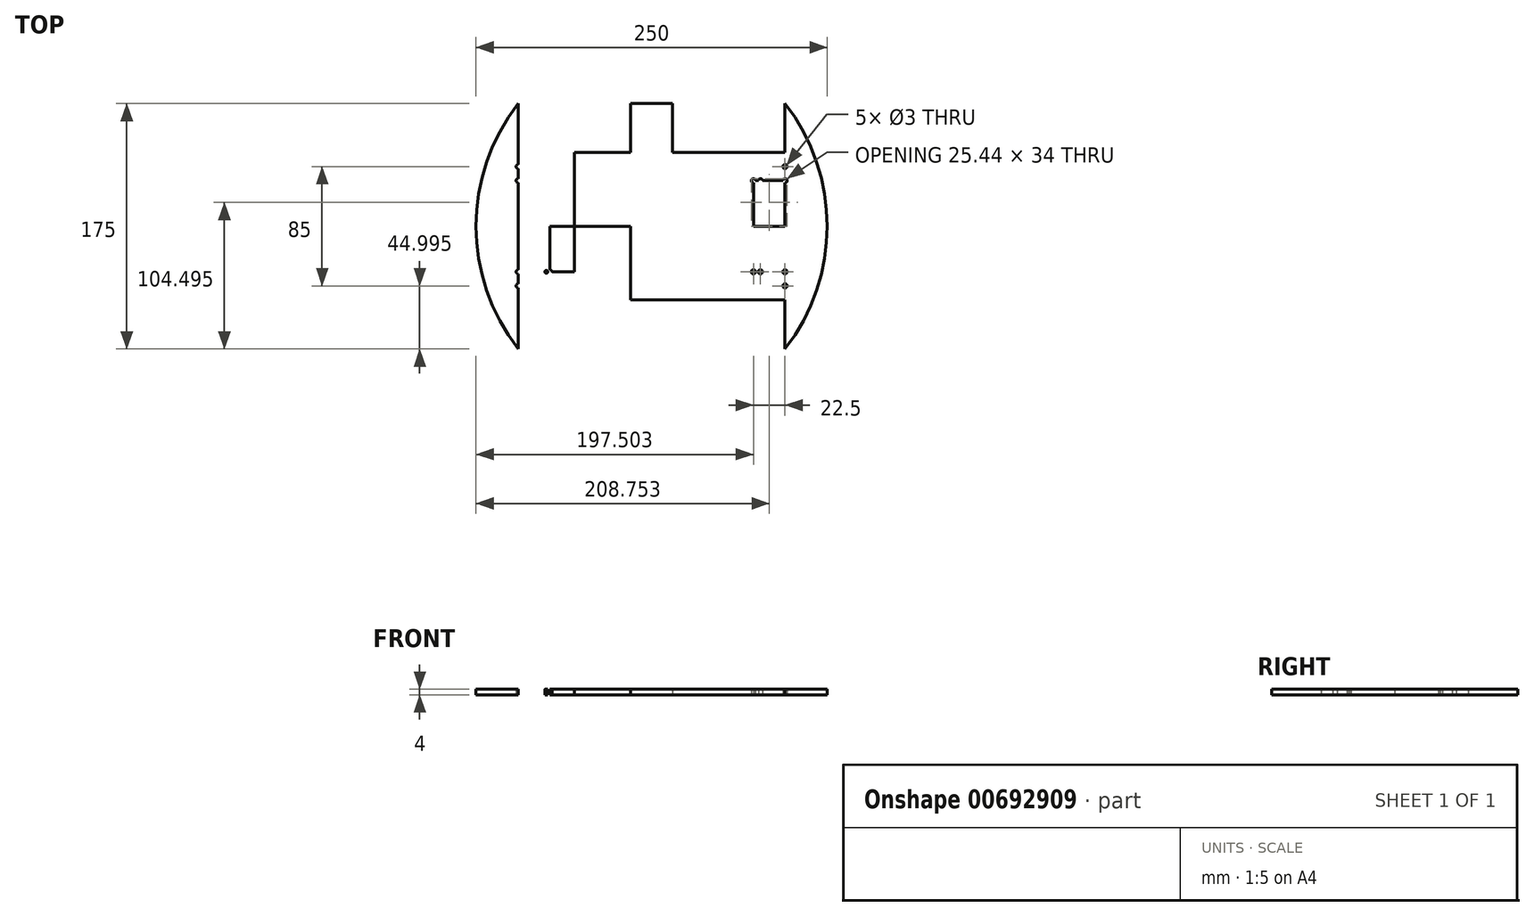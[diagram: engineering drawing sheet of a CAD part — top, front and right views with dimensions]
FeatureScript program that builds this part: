
annotation { "Feature Type Name" : "Feature", "Feature Type Description" : "" }
export const myFeature = defineFeature(function(context is Context, id is Id, definition is map)
    precondition{}
    {
        {
            var Q0;
            Q0=qCreatedBy(makeId("Top.planeOp"),FACE);
            var sketch = newSketch(context, id + "F0", { "sketchPlane" : qUnion([Q0])});
            skLineSegment(sketch, "E0", {"start": v(-125.28, 50.29) * mm, "end": v(-45.28, 50.29) * mm});
            skLineSegment(sketch, "E1", {"start": v(-45.28, 50.29) * mm, "end": v(-45.28, 85.29) * mm});
            skLineSegment(sketch, "E2", {"start": v(-45.28, 85.29) * mm, "end": v(-15.28, 85.29) * mm});
            skLineSegment(sketch, "E3", {"start": v(-15.28, 85.29) * mm, "end": v(-15.28, 50.29) * mm});
            skLineSegment(sketch, "E4", {"start": v(-15.28, 50.29) * mm, "end": v(64.72, 50.29) * mm});
            skLineSegment(sketch, "E5", {"start": v(64.72, 50.29) * mm, "end": v(64.72, 85.29) * mm});
            skLineSegment(sketch, "E6", {"start": v(-125.28, 50.29) * mm, "end": v(-125.28, 85.29) * mm});
            skLineSegment(sketch, "E7", {"start": v(-45.28, -54.71) * mm, "end": v(-45.28, 50.29) * mm});
            skLineSegment(sketch, "E8", {"start": v(-45.28, -54.71) * mm, "end": v(-125.28, -54.71) * mm});
            skLineSegment(sketch, "E9", {"start": v(-125.28, -54.71) * mm, "end": v(-125.28, 50.29) * mm});
            skLineSegment(sketch, "E10", {"start": v(-15.28, 50.29) * mm, "end": v(-15.28, -54.71) * mm});
            skLineSegment(sketch, "E11", {"start": v(-15.28, -54.71) * mm, "end": v(-45.28, -54.71) * mm});
            skLineSegment(sketch, "E12", {"start": v(-45.28, 50.29) * mm, "end": v(-15.28, 50.29) * mm});
            skLineSegment(sketch, "E13", {"start": v(64.72, 50.29) * mm, "end": v(64.72, -54.71) * mm});
            skLineSegment(sketch, "E14", {"start": v(64.72, -54.71) * mm, "end": v(-15.28, -54.71) * mm});
            skLineSegment(sketch, "E15.bottom", {"start": v(-45.28, -54.71) * mm, "end": v(-15.33, -54.71) * mm});
            skLineSegment(sketch, "E15.top", {"start": v(-45.28, -89.71) * mm, "end": v(-15.33, -89.71) * mm});
            skLineSegment(sketch, "E15.left", {"start": v(-45.28, -54.71) * mm, "end": v(-45.28, -89.71) * mm});
            skLineSegment(sketch, "E15.right", {"start": v(-15.33, -54.71) * mm, "end": v(-15.33, -89.71) * mm});
            skLineSegment(sketch, "E16", {"start": v(-125.28, -54.71) * mm, "end": v(-125.28, -89.71) * mm});
            skArc(sketch, "E17", {"start": v(-125.28, 85.29) * mm, "mid": v(-155.28, -2.21) * mm, "end": v(-125.28, -89.71) * mm});
            skLineSegment(sketch, "E18", {"start": v(64.72, -54.71) * mm, "end": v(64.72, -89.71) * mm});
            skArc(sketch, "E19", {"start": v(64.72, -89.71) * mm, "mid": v(94.72, -2.21) * mm, "end": v(64.72, 85.29) * mm});
            skLineSegment(sketch, "E20", {"start": v(-125.28, -54.71) * mm, "end": v(-85.28, -54.71) * mm});
            skLineSegment(sketch, "E21", {"start": v(-85.28, -54.71) * mm, "end": v(-45.28, -54.71) * mm});
            skLineSegment(sketch, "E22", {"start": v(-85.28, -54.71) * mm, "end": v(-85.28, 50.29) * mm});
            skLineSegment(sketch, "E23", {"start": v(-85.28, 50.29) * mm, "end": v(-45.28, 50.29) * mm});
            skLineSegment(sketch, "E24", {"start": v(-85.28, 50.29) * mm, "end": v(-125.28, 50.29) * mm});
            skLineSegment(sketch, "E25", {"start": v(-85.28, -54.71) * mm, "end": v(-85.28, -34.71) * mm});
            skLineSegment(sketch, "E26", {"start": v(-85.28, -34.71) * mm, "end": v(-105.28, -34.71) * mm});
            skCircle(sketch, "E27", {"center": v(-105.28, -34.71) * mm, "radius": 1 * mm});
            skPoint(sketch, "E28", {"position": v(-104.28, -34.71) * mm});
            skLineSegment(sketch, "E29", {"start": v(-104.28, -34.71) * mm, "end": v(-102.78, -34.71) * mm});
            skCircle(sketch, "E30", {"center": v(-102.78, -34.71) * mm, "radius": 1.5 * mm});
            skLineSegment(sketch, "E31", {"start": v(-105.28, -34.71) * mm, "end": v(-106.28, -34.71) * mm});
            skLineSegment(sketch, "E32", {"start": v(-106.28, -34.71) * mm, "end": v(-107.78, -34.71) * mm});
            skCircle(sketch, "E33", {"center": v(-107.78, -34.71) * mm, "radius": 1.5 * mm});
            skLineSegment(sketch, "E34", {"start": v(-30.28, 50.29) * mm, "end": v(-30.28, -2.21) * mm});
            skLineSegment(sketch, "E35", {"start": v(-30.28, -2.21) * mm, "end": v(-155.28, -2.21) * mm});
            skLineSegment(sketch, "E36", {"start": v(-30.28, -2.21) * mm, "end": v(94.72, -2.21) * mm});
            skLineSegment(sketch, "E37", {"start": v(94.72, -2.21) * mm, "end": v(-155.28, -2.21) * mm});
            skLineSegment(sketch, "E38", {"start": v(-107.78, -34.71) * mm, "end": v(-107.78, 30.29) * mm});
            skCircle(sketch, "E39", {"center": v(-107.78, 30.29) * mm, "radius": 1.5 * mm});
            skLineSegment(sketch, "E40", {"start": v(-102.78, -34.71) * mm, "end": v(-102.78, 30.29) * mm});
            skCircle(sketch, "E41", {"center": v(-102.78, 30.29) * mm, "radius": 1.5 * mm});
            skLineSegment(sketch, "E42", {"start": v(64.72, 50.29) * mm, "end": v(64.72, 30.29) * mm});
            skLineSegment(sketch, "E43", {"start": v(64.72, 30.29) * mm, "end": v(47.22, 30.29) * mm});
            skCircle(sketch, "E44", {"center": v(47.22, 30.29) * mm, "radius": 1.5 * mm});
            skLineSegment(sketch, "E45", {"start": v(47.22, 30.29) * mm, "end": v(42.22, 30.29) * mm});
            skCircle(sketch, "E46", {"center": v(42.22, 30.29) * mm, "radius": 1.5 * mm});
            skLineSegment(sketch, "E47", {"start": v(42.22, 30.29) * mm, "end": v(42.22, -34.71) * mm});
            skCircle(sketch, "E48", {"center": v(42.22, -34.71) * mm, "radius": 1.5 * mm});
            skLineSegment(sketch, "E49", {"start": v(47.22, 30.29) * mm, "end": v(47.22, -34.71) * mm});
            skCircle(sketch, "E50", {"center": v(47.22, -34.71) * mm, "radius": 1.5 * mm});
            skLineSegment(sketch, "E51", {"start": v(-75, 45.86) * mm, "end": v(0, 45.86) * mm});
            skLineSegment(sketch, "E52", {"start": v(-125.28, 50.29) * mm, "end": v(-125.28, 30.29) * mm});
            skCircle(sketch, "E53", {"center": v(-125.28, 30.29) * mm, "radius": 1.5 * mm});
            skLineSegment(sketch, "E54", {"start": v(-125.28, 30.29) * mm, "end": v(-125.28, 40.29) * mm});
            skCircle(sketch, "E55", {"center": v(-125.28, 40.29) * mm, "radius": 1.5 * mm});
            skLineSegment(sketch, "E56", {"start": v(-125.28, -54.71) * mm, "end": v(-125.28, -34.71) * mm});
            skCircle(sketch, "E57", {"center": v(-125.28, -34.71) * mm, "radius": 1.5 * mm});
            skLineSegment(sketch, "E58", {"start": v(-125.28, -34.71) * mm, "end": v(-125.28, -44.71) * mm});
            skCircle(sketch, "E59", {"center": v(-125.28, -44.71) * mm, "radius": 1.5 * mm});
            skCircle(sketch, "E60", {"center": v(64.72, 30.29) * mm, "radius": 1.5 * mm});
            skLineSegment(sketch, "E61", {"start": v(64.72, 30.29) * mm, "end": v(64.72, 40.29) * mm});
            skCircle(sketch, "E62", {"center": v(64.72, 40.29) * mm, "radius": 1.5 * mm});
            skLineSegment(sketch, "E63", {"start": v(64.72, -54.71) * mm, "end": v(64.72, -34.71) * mm});
            skCircle(sketch, "E64", {"center": v(64.72, -34.71) * mm, "radius": 1.5 * mm});
            skLineSegment(sketch, "E65", {"start": v(64.72, -34.71) * mm, "end": v(64.72, -44.71) * mm});
            skCircle(sketch, "E66", {"center": v(64.72, -44.71) * mm, "radius": 1.5 * mm});
            skSolve(sketch);
        }
        {
            var Q0;
            Q0=makeQuery(id+"F0.imprint","IMPRINT",FACE,{"disambiguationData":[TD([[makeQuery(id+"F0.imprint","IMPRINT",EDGE,{"derivedFrom":sQuery(id+"F0.wireOp",EDGE,"E6")}),1.0]])]});
            var Q1;
            Q1=makeQuery(id+"F0.imprint","IMPRINT",FACE,{"disambiguationData":[TD([[makeQuery(id+"F0.imprint","IMPRINT",EDGE,{"derivedFrom":sQuery(id+"F0.wireOp",EDGE,"E0")}),-1.0]])]});
            var Q2;
            Q2=makeQuery(id+"F0.imprint","IMPRINT",FACE,{"disambiguationData":[TD([[makeQuery(id+"F0.imprint","IMPRINT",EDGE,{"derivedFrom":sQuery(id+"F0.wireOp",EDGE,"E7")}),-1.0]])]});
            var Q3;
            Q3=makeQuery(id+"F0.imprint","IMPRINT",FACE,{"disambiguationData":[TD([[makeQuery(id+"F0.imprint","IMPRINT",EDGE,{"derivedFrom":sQuery(id+"F0.wireOp",EDGE,"E1")}),-1.0]])]});
            var Q4;
            Q4=makeQuery(id+"F0.imprint","IMPRINT",FACE,{"disambiguationData":[TD([[makeQuery(id+"F0.imprint","IMPRINT",EDGE,{"derivedFrom":sQuery(id+"F0.wireOp",EDGE,"E15.bottom")}),-1.0]])]});
            var Q5;
            Q5=makeQuery(id+"F0.imprint","IMPRINT",FACE,{"disambiguationData":[TD([[makeQuery(id+"F0.imprint","IMPRINT",EDGE,{"derivedFrom":sQuery(id+"F0.wireOp",EDGE,"E4")}),-1.0]])]});
            var Q6;
            Q6=makeQuery(id+"F0.imprint","IMPRINT",FACE,{"disambiguationData":[TD([[makeQuery(id+"F0.imprint","IMPRINT",EDGE,{"derivedFrom":sQuery(id+"F0.wireOp",EDGE,"E5")}),-1.0]])]});
            var Q7;
            {var subQ0=sQuery(id+"F0.wireOp",EDGE,"E16");Q7=makeQuery(id+"F0.imprint","IMPRINT",FACE,{"disambiguationData":[TD([[makeQuery(id+"F0.imprint","IMPRINT",EDGE,{"derivedFrom":subQ0}),-1.0]])]});}
            var Q8;
            {var subQ0=sQuery(id+"F0.wireOp",EDGE,"E24");Q8=makeQuery(id+"F0.imprint","IMPRINT",FACE,{"disambiguationData":[TD([[makeQuery(id+"F0.imprint","IMPRINT",EDGE,{"derivedFrom":subQ0}),1.0]])]});}
            var Q9;
            {var subQ4=sQuery(id+"F0.wireOp",EDGE,"E21");Q9=makeQuery(id+"F0.imprint","IMPRINT",FACE,{"disambiguationData":[TD([[makeQuery(id+"F0.imprint","IMPRINT",EDGE,{"derivedFrom":subQ4}),1.0]])]});}
            var Q10;
            {var subQ1=sQuery(id+"F0.wireOp",EDGE,"E11");Q10=makeQuery(id+"F0.imprint","IMPRINT",FACE,{"disambiguationData":[TD([[makeQuery(id+"F0.imprint","IMPRINT",EDGE,{"derivedFrom":subQ1}),-1.0]])]});}
            var Q11;
            {var subQ5=sQuery(id+"F0.wireOp",EDGE,"E34");Q11=makeQuery(id+"F0.imprint","IMPRINT",FACE,{"disambiguationData":[TD([[makeQuery(id+"F0.imprint","IMPRINT",EDGE,{"derivedFrom":subQ5}),1.0]])]});}
            var Q12;
            {var subQ0=sQuery(id+"F0.wireOp",EDGE,"E23");Q12=makeQuery(id+"F0.imprint","IMPRINT",FACE,{"disambiguationData":[TD([[makeQuery(id+"F0.imprint","IMPRINT",EDGE,{"derivedFrom":subQ0}),-1.0]])]});}
            var Q13;
            {var subQ0=sQuery(id+"F0.wireOp",EDGE,"E14");Q13=makeQuery(id+"F0.imprint","IMPRINT",FACE,{"disambiguationData":[TD([[makeQuery(id+"F0.imprint","IMPRINT",EDGE,{"derivedFrom":subQ0}),-1.0]])]});}
            var Q14;
            {var subQ0=sQuery(id+"F0.wireOp",EDGE,"E18");Q14=makeQuery(id+"F0.imprint","IMPRINT",FACE,{"disambiguationData":[TD([[makeQuery(id+"F0.imprint","IMPRINT",EDGE,{"derivedFrom":subQ0}),1.0]])]});}
            extrude(context, id + "F1", {"entities" : qUnion([Q0, Q1, Q2, Q3, Q4, Q5, Q6, Q7, Q8, Q9, Q10, Q11, Q12, Q13, Q14]), "depth" : 4 * mm, "offsetDistance" : 25 * mm});
        }
        {
            var Q0;
            {var subQ4=sQuery(id+"F0.wireOp",EDGE,"E20");Q0=makeQuery(id+"F0.imprint","IMPRINT",FACE,{"disambiguationData":[TD([[makeQuery(id+"F0.imprint","IMPRINT",EDGE,{"derivedFrom":subQ4}),1.0]])]});}
            var Q1;
            {var subQ0=sQuery(id+"F0.wireOp",EDGE,"E31");Q1=makeQuery(id+"F0.imprint","IMPRINT",FACE,{"disambiguationData":[TD([[makeQuery(id+"F0.imprint","IMPRINT",EDGE,{"derivedFrom":subQ0}),1.0]])]});}
            var Q2;
            {var subQ0=sQuery(id+"F0.wireOp",EDGE,"E31");Q2=makeQuery(id+"F0.imprint","IMPRINT",FACE,{"disambiguationData":[TD([[makeQuery(id+"F0.imprint","IMPRINT",EDGE,{"derivedFrom":subQ0}),-1.0]])]});}
            var Q3;
            {var subQ0=sQuery(id+"F0.wireOp",EDGE,"E40");var subQ1=sQuery(id+"F0.wireOp",EDGE,"E37");var subQ2=makeQuery(id+"F0.imprint","INTERSECT",VERTEX,{"derivedFrom":[subQ1,subQ0]});Q3=makeQuery(id+"F0.imprint","IMPRINT",FACE,{"disambiguationData":[TD([[makeQuery(id+"F0.imprint","IMPRINT",EDGE,{"disambiguationData":[TD([[subQ2,-1.0]])],"derivedFrom":subQ1}),1.0]])]});}
            var Q4;
            {var subQ5=sQuery(id+"F0.wireOp",EDGE,"E30");var subQ6=sQuery(id+"F0.wireOp",EDGE,"E26");var subQ7=makeQuery(id+"F0.imprint","INTERSECT",VERTEX,{"derivedFrom":[subQ6,subQ5]});Q4=makeQuery(id+"F0.imprint","IMPRINT",FACE,{"disambiguationData":[TD([[makeQuery(id+"F0.imprint","IMPRINT",EDGE,{"disambiguationData":[TD([[subQ7,-1.0]])],"derivedFrom":subQ5}),-1.0]])]});}
            var Q5;
            {var subQ3=sQuery(id+"F0.wireOp",EDGE,"E49");var subQ7=sQuery(id+"F0.wireOp",EDGE,"E37");var subQ8=makeQuery(id+"F0.imprint","INTERSECT",VERTEX,{"derivedFrom":[subQ7,subQ3]});Q5=makeQuery(id+"F0.imprint","IMPRINT",FACE,{"disambiguationData":[TD([[makeQuery(id+"F0.imprint","IMPRINT",EDGE,{"disambiguationData":[TD([[subQ8,1.0]])],"derivedFrom":subQ7}),-1.0]])]});}
            var Q6;
            {var subQ5=sQuery(id+"F0.wireOp",EDGE,"E49");var subQ6=sQuery(id+"F0.wireOp",EDGE,"E37");var subQ7=makeQuery(id+"F0.imprint","INTERSECT",VERTEX,{"derivedFrom":[subQ6,subQ5]});Q6=makeQuery(id+"F0.imprint","IMPRINT",FACE,{"disambiguationData":[TD([[makeQuery(id+"F0.imprint","IMPRINT",EDGE,{"disambiguationData":[TD([[subQ7,-1.0]])],"derivedFrom":subQ6}),-1.0]])]});}
            extrude(context, id + "F2", {"entities" : qUnion([Q0, Q1, Q2, Q3, Q4, Q5, Q6]), "operationType" : NewBodyOperationType.ADD, "depth" : 4 * mm, "offsetDistance" : 25 * mm});
        }
    });
